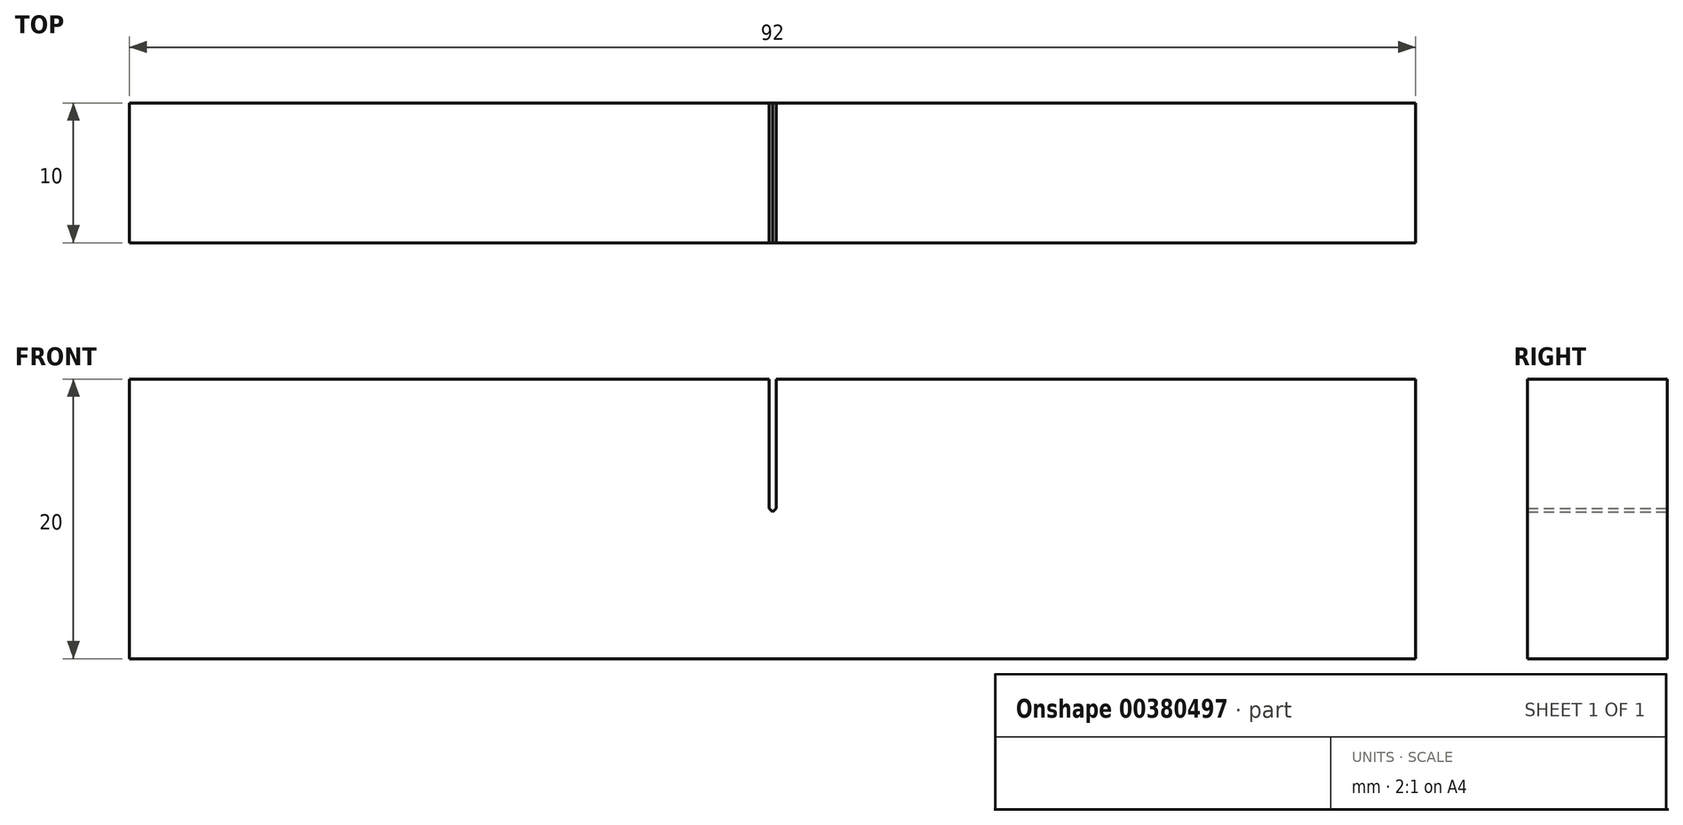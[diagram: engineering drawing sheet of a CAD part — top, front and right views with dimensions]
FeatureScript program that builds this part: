
annotation { "Feature Type Name" : "Feature", "Feature Type Description" : "" }
export const myFeature = defineFeature(function(context is Context, id is Id, definition is map)
    precondition{}
    {
        {
            var Q0;
            Q0=qCreatedBy(makeId("Front.planeOp"),FACE);
            var sketch = newSketch(context, id + "F0", { "sketchPlane" : qUnion([Q0])});
            skLineSegment(sketch, "E0", {"start": v(-46, 0) * mm, "end": v(-46, 20) * mm});
            skLineSegment(sketch, "E1", {"start": v(-46, 20) * mm, "end": v(-0.25, 20) * mm});
            skLineSegment(sketch, "E2", {"start": v(-0.25, 20) * mm, "end": v(-0.25, 10.75) * mm});
            skLineSegment(sketch, "E3", {"start": v(-0.25, 10.75) * mm, "end": v(0, 10.5) * mm});
            skLineSegment(sketch, "E4", {"start": v(0, 10.5) * mm, "end": v(0.25, 10.75) * mm});
            skLineSegment(sketch, "E5", {"start": v(0.25, 10.75) * mm, "end": v(0.25, 20) * mm});
            skLineSegment(sketch, "E6", {"start": v(0.25, 20) * mm, "end": v(46, 20) * mm});
            skLineSegment(sketch, "E7", {"start": v(46, 20) * mm, "end": v(46, 0) * mm});
            skLineSegment(sketch, "E8", {"start": v(46, 0) * mm, "end": v(-46, 0) * mm});
            skSolve(sketch);
        }
        {
            var Q0;
            Q0 = qSketchRegion(id + "F0", true);
            extrude(context, id + "F1", {"entities" : qUnion([Q0]), "depth" : 10 * mm});
        }
    });
